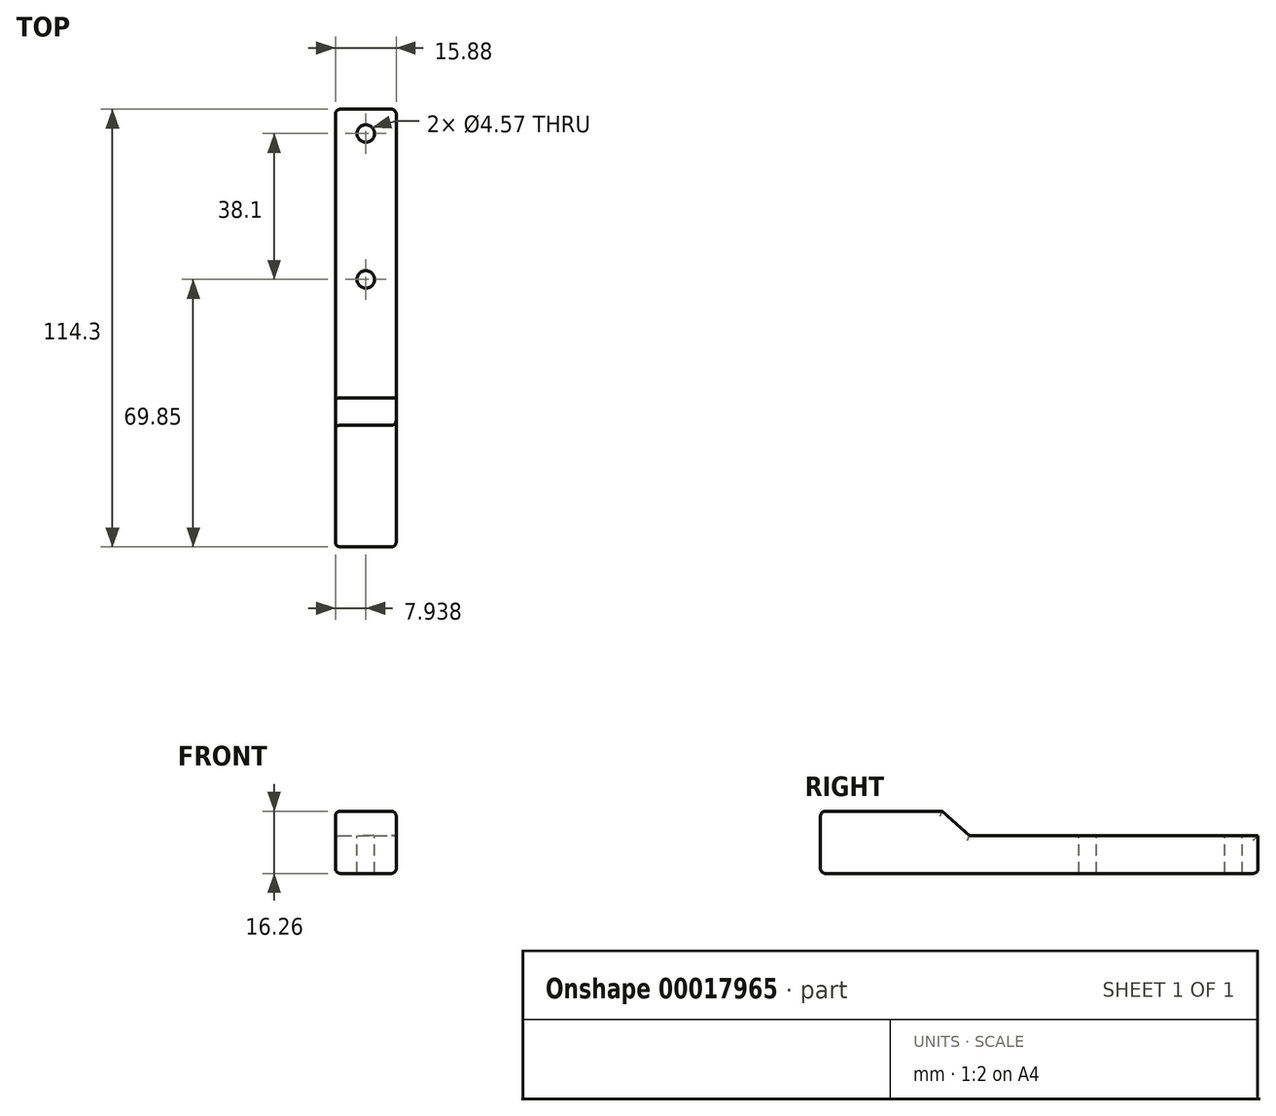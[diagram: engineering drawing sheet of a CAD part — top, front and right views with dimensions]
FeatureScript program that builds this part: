
annotation { "Feature Type Name" : "Feature", "Feature Type Description" : "" }
export const myFeature = defineFeature(function(context is Context, id is Id, definition is map)
    precondition{}
    {
        {
            var Q0;
            Q0=qCreatedBy(makeId("Top.planeOp"),FACE);
            var sketch = newSketch(context, id + "F0", { "sketchPlane" : qUnion([Q0])});
            skLineSegment(sketch, "E0.bottom", {"start": v(0, 0) * mm, "end": v(15.88, 0) * mm});
            skLineSegment(sketch, "E0.top", {"start": v(0, -114.3) * mm, "end": v(15.88, -114.3) * mm});
            skLineSegment(sketch, "E0.left", {"start": v(0, 0) * mm, "end": v(0, -114.3) * mm});
            skLineSegment(sketch, "E0.right", {"start": v(15.88, 0) * mm, "end": v(15.88, -114.3) * mm});
            skSolve(sketch);
        }
        {
            var Q0;
            Q0=makeQuery(id+"F0.imprint","IMPRINT",FACE,{"disambiguationData":[TD([[makeQuery(id+"F0.imprint","IMPRINT",EDGE,{"derivedFrom":sQuery(id+"F0.wireOp",EDGE,"E0.bottom")}),-1.0]])]});
            extrude(context, id + "F1", {"entities" : qUnion([Q0]), "depth" : 16.26 * mm, "offsetDistance" : 25.4 * mm});
        }
        {
            var Q0;
            Q0=makeQuery(id+"F1.opExtrude","SWEPT_FACE",FACE,{"disambiguationData":[OSD([sQuery(id+"F0.wireOp",EDGE,"E0.right")])]});
            var sketch = newSketch(context, id + "F2", { "sketchPlane" : qUnion([Q0])});
            skLineSegment(sketch, "E1", {"start": v(0, 9.9) * mm, "end": v(-75.4, 9.9) * mm});
            skLineSegment(sketch, "E2", {"start": v(-75.4, 9.9) * mm, "end": v(-82.55, 16.26) * mm});
            skSolve(sketch);
        }
        {
            var Q0;
            {var subQ0=sQuery(id+"F2.wireOp",EDGE,"E1");Q0=makeQuery(id+"F2.imprint","IMPRINT",FACE,{"disambiguationData":[TD([[makeQuery(id+"F2.imprint","IMPRINT",EDGE,{"derivedFrom":subQ0}),-1.0]])]});}
            extrude(context, id + "F3", {"entities" : qUnion([Q0]), "operationType" : NewBodyOperationType.REMOVE, "oppositeDirection" : true, "offsetDistance" : 25.4 * mm, "depth" : 25.4 * mm});
        }
        {
            var Q0;
            Q0=makeQuery(id+"F3.boolean.opBoolean","COPY",FACE,{"derivedFrom":makeQuery(id+"F3.opExtrude","SWEPT_FACE",FACE,{"disambiguationData":[OSD([sQuery(id+"F2.wireOp",EDGE,"E1")])]})});
            var sketch = newSketch(context, id + "F4", { "sketchPlane" : qUnion([Q0])});
            skCircle(sketch, "E3", {"center": v(7.94, -6.35) * mm, "radius": 2.29 * mm});
            skPoint(sketch, "E3.centerSnap0", {"position": v(7.94, 0) * mm});
            skCircle(sketch, "E4", {"center": v(7.94, -44.45) * mm, "radius": 2.29 * mm});
            skSolve(sketch);
        }
        {
            var Q0;
            Q0=makeQuery(id+"F4.imprint","IMPRINT",FACE,{"disambiguationData":[TD([[makeQuery(id+"F4.imprint","IMPRINT",EDGE,{"derivedFrom":sQuery(id+"F4.wireOp",EDGE,"E3")}),1.0]])]});
            var Q1;
            Q1=makeQuery(id+"F4.imprint","IMPRINT",FACE,{"disambiguationData":[TD([[makeQuery(id+"F4.imprint","IMPRINT",EDGE,{"derivedFrom":sQuery(id+"F4.wireOp",EDGE,"E4")}),1.0]])]});
            extrude(context, id + "F5", {"entities" : qUnion([Q0, Q1]), "operationType" : NewBodyOperationType.REMOVE, "oppositeDirection" : true, "offsetDistance" : 25.4 * mm, "depth" : 25.4 * mm});
        }
        {
            var Q0;
            Q0=makeQuery(id+"F1.opExtrude","CAP_EDGE",EDGE,{"disambiguationData":[OSD([sQuery(id+"F0.wireOp",EDGE,"E0.top")])],"isStart":true});
            var Q1;
            Q1=makeQuery(id+"F1.opExtrude","SWEPT_EDGE",EDGE,{"disambiguationData":[OSD([sQuery(id+"F0.wireOp",EDGE,"E0.top"),sQuery(id+"F0.wireOp",EDGE,"E0.left")])]});
            var Q2;
            Q2=makeQuery(id+"F1.opExtrude","SWEPT_EDGE",EDGE,{"disambiguationData":[OSD([sQuery(id+"F0.wireOp",EDGE,"E0.top"),sQuery(id+"F0.wireOp",EDGE,"E0.right")])]});
            var Q3;
            Q3=makeQuery(id+"F1.opExtrude","CAP_EDGE",EDGE,{"disambiguationData":[OSD([sQuery(id+"F0.wireOp",EDGE,"E0.top")])],"isStart":false});
            var Q4;
            Q4=makeQuery(id+"F1.opExtrude","CAP_EDGE",EDGE,{"disambiguationData":[OSD([sQuery(id+"F0.wireOp",EDGE,"E0.left")])],"isStart":true});
            var Q5;
            Q5=makeQuery(id+"F1.opExtrude","CAP_EDGE",EDGE,{"disambiguationData":[OSD([sQuery(id+"F0.wireOp",EDGE,"E0.right")])],"isStart":true});
            var Q6;
            Q6=makeQuery(id+"F1.opExtrude","CAP_EDGE",EDGE,{"disambiguationData":[OSD([sQuery(id+"F0.wireOp",EDGE,"E0.bottom")])],"isStart":true});
            var Q7;
            Q7=makeQuery(id+"F3.boolean.opBoolean","INTERSECT",EDGE,{"derivedFrom":[makeQuery(id+"F1.opExtrude","SWEPT_FACE",FACE,{"disambiguationData":[OSD([sQuery(id+"F0.wireOp",EDGE,"E0.left")])]}),makeQuery(id+"F3.opExtrude","SWEPT_FACE",FACE,{"disambiguationData":[OSD([sQuery(id+"F2.wireOp",EDGE,"E1")])]})]});
            var Q8;
            Q8=makeQuery(id+"F3.boolean.opBoolean","COPY",EDGE,{"derivedFrom":makeQuery(id+"F3.opExtrude","CAP_EDGE",EDGE,{"disambiguationData":[OSD([sQuery(id+"F2.wireOp",EDGE,"E1")])],"isStart":true})});
            var Q9;
            Q9=makeQuery(id+"F3.boolean.opBoolean","COPY",EDGE,{"derivedFrom":makeQuery(id+"F3.opExtrude","SWEPT_EDGE",EDGE,{"disambiguationData":[OSD([sQuery(id+"F0.wireOp",EDGE,"E0.bottom"),sQuery(id+"F0.wireOp",EDGE,"E0.right"),sQuery(id+"F2.wireOp",EDGE,"E1")])]})});
            var Q10;
            Q10=makeQuery(id+"F1.opExtrude","SWEPT_EDGE",EDGE,{"disambiguationData":[OSD([sQuery(id+"F0.wireOp",EDGE,"E0.bottom"),sQuery(id+"F0.wireOp",EDGE,"E0.right")])]});
            var Q11;
            Q11=makeQuery(id+"F1.opExtrude","SWEPT_EDGE",EDGE,{"disambiguationData":[OSD([sQuery(id+"F0.wireOp",EDGE,"E0.bottom"),sQuery(id+"F0.wireOp",EDGE,"E0.left")])]});
            var Q12;
            Q12=makeQuery(id+"F3.boolean.opBoolean","INTERSECT",EDGE,{"derivedFrom":[makeQuery(id+"F1.opExtrude","SWEPT_FACE",FACE,{"disambiguationData":[OSD([sQuery(id+"F0.wireOp",EDGE,"E0.left")])]}),makeQuery(id+"F3.opExtrude","SWEPT_FACE",FACE,{"disambiguationData":[OSD([sQuery(id+"F2.wireOp",EDGE,"E2")])]})]});
            var Q13;
            Q13=makeQuery(id+"F3.boolean.opBoolean","COPY",EDGE,{"derivedFrom":makeQuery(id+"F3.opExtrude","SWEPT_EDGE",EDGE,{"disambiguationData":[OSD([sQuery(id+"F0.wireOp",EDGE,"E0.right"),sQuery(id+"F2.wireOp",EDGE,"E2")])]})});
            var Q14;
            Q14=makeQuery(id+"F3.boolean.opBoolean","COPY",EDGE,{"derivedFrom":makeQuery(id+"F3.opExtrude","CAP_EDGE",EDGE,{"disambiguationData":[OSD([sQuery(id+"F2.wireOp",EDGE,"E2")])],"isStart":true})});
            var Q15;
            Q15=makeQuery(id+"F1.opExtrude","CAP_EDGE",EDGE,{"disambiguationData":[OSD([sQuery(id+"F0.wireOp",EDGE,"E0.right")])],"isStart":false});
            var Q16;
            Q16=makeQuery(id+"F1.opExtrude","CAP_EDGE",EDGE,{"disambiguationData":[OSD([sQuery(id+"F0.wireOp",EDGE,"E0.left")])],"isStart":false});
            fillet(context, id + "F6", {"entities" : qUnion([Q0, Q1, Q2, Q3, Q4, Q5, Q6, Q7, Q8, Q9, Q10, Q11, Q12, Q13, Q14, Q15, Q16]), "radius" : 1.27 * mm, "tangentPropagation" : true, "defaultsChanged" : false, "vertexSettings" : [], "allowEdgeOverflow" : false});
        }
    });
